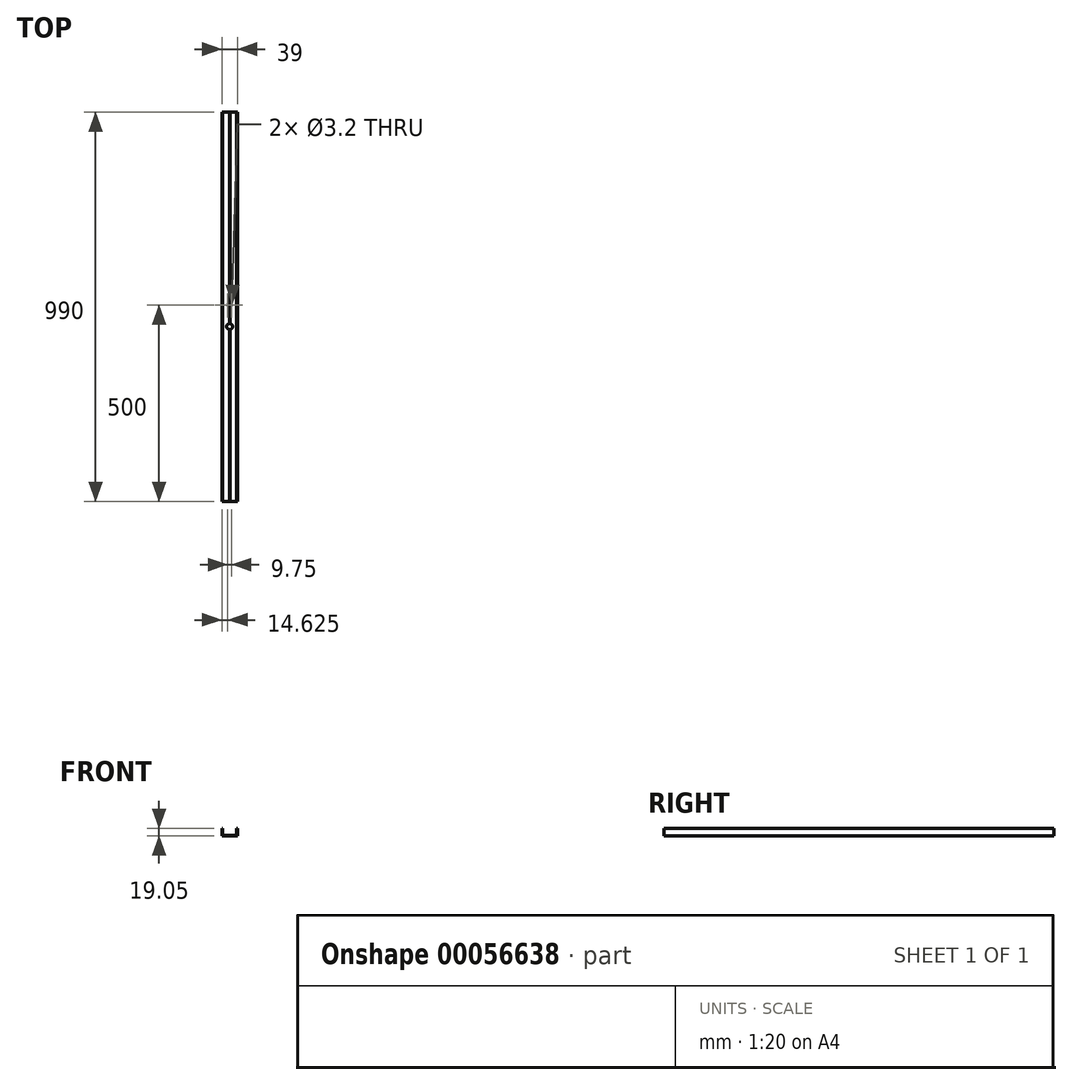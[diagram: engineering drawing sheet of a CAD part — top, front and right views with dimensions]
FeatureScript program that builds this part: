
annotation { "Feature Type Name" : "Feature", "Feature Type Description" : "" }
export const myFeature = defineFeature(function(context is Context, id is Id, definition is map)
    precondition{}
    {
        {
            var Q0;
            Q0=qCreatedBy(makeId("Front.planeOp"),FACE);
            var sketch = newSketch(context, id + "F0", { "sketchPlane" : qUnion([Q0])});
            skLineSegment(sketch, "E0", {"start": v(-19.5, 0) * mm, "end": v(-19.5, 19.05) * mm});
            skLineSegment(sketch, "E1", {"start": v(-18, 19.05) * mm, "end": v(-18, 1.5) * mm});
            skLineSegment(sketch, "E2", {"start": v(-0.45, 1.5) * mm, "end": v(-18, 1.5) * mm});
            skLineSegment(sketch, "E3", {"start": v(-0.45, 1.5) * mm, "end": v(-0.45, 0) * mm});
            skLineSegment(sketch, "E4", {"start": v(-19.5, 0) * mm, "end": v(-0.45, 0) * mm});
            skLineSegment(sketch, "E5", {"start": v(-19.5, 19.05) * mm, "end": v(-18, 19.05) * mm});
            skLineSegment(sketch, "E6", {"start": v(0, 0) * mm, "end": v(0, 19.05) * mm, "construction": true});
            skLineSegment(sketch, "E7.MirrorCS", {"start": v(19.5, 0) * mm, "end": v(19.5, 19.05) * mm});
            skLineSegment(sketch, "E8.MirrorCS", {"start": v(19.5, 19.05) * mm, "end": v(18, 19.05) * mm});
            skLineSegment(sketch, "E9.MirrorCS", {"start": v(18, 19.05) * mm, "end": v(18, 1.5) * mm});
            skLineSegment(sketch, "E10.MirrorCS", {"start": v(0.45, 1.5) * mm, "end": v(18, 1.5) * mm});
            skLineSegment(sketch, "E11.MirrorCS", {"start": v(0.45, 1.5) * mm, "end": v(0.45, 0) * mm});
            skLineSegment(sketch, "E12.MirrorCS", {"start": v(19.5, 0) * mm, "end": v(0.45, 0) * mm});
            skSolve(sketch);
        }
        {
            var Q0;
            Q0 = qSketchRegion(id + "F0", true);
            extrude(context, id + "F1", {"entities" : qUnion([Q0]), "depth" : (1000 - 5 * 2) * mm, "symmetric" : true});
        }
        {
            var Q0;
            Q0=makeQuery(id+"F1.opExtrude","SWEPT_FACE",FACE,{"disambiguationData":[OSD([sQuery(id+"F0.wireOp",EDGE,"E2")])]});
            var sketch = newSketch(context, id + "F2", { "sketchPlane" : qUnion([Q0])});
            skLineSegment(sketch, "E13", {"start": v(0, 5) * mm, "end": v(-4.88, 5) * mm, "construction": true});
            skLineSegment(sketch, "E14", {"start": v(0, 5) * mm, "end": v(4.87, 5) * mm, "construction": true});
            skCircle(sketch, "E15", {"center": v(-4.88, 5) * mm, "radius": 1.6 * mm});
            skCircle(sketch, "E16", {"center": v(4.87, 5) * mm, "radius": 1.6 * mm});
            skLineSegment(sketch, "E17", {"start": v(0, 0) * mm, "end": v(0, 5) * mm, "construction": true});
            skSolve(sketch);
        }
        {
            var Q0;
            Q0 = qSketchRegion(id + "F2", true);
            extrude(context, id + "F3", {"entities" : qUnion([Q0]), "operationType" : NewBodyOperationType.REMOVE, "endBound" : BoundingType.THROUGH_ALL, "oppositeDirection" : true, "depth" : 25 * mm});
        }
        {
            var Q0;
            Q0=makeQuery(id+"F1.opExtrude","SWEPT_FACE",FACE,{"disambiguationData":[OSD([sQuery(id+"F0.wireOp",EDGE,"E2")])]});
            var sketch = newSketch(context, id + "F4", { "sketchPlane" : qUnion([Q0])});
            skLineSegment(sketch, "E18", {"start": v(0, 0) * mm, "end": v(0, -50) * mm, "construction": true});
            skCircle(sketch, "E19", {"center": v(0, -50) * mm, "radius": 7.5 * mm});
            skSolve(sketch);
        }
        {
            var Q0;
            Q0 = qSketchRegion(id + "F4", true);
            extrude(context, id + "F5", {"entities" : qUnion([Q0]), "operationType" : NewBodyOperationType.REMOVE, "endBound" : BoundingType.THROUGH_ALL, "oppositeDirection" : true, "depth" : 25 * mm});
        }
    });
